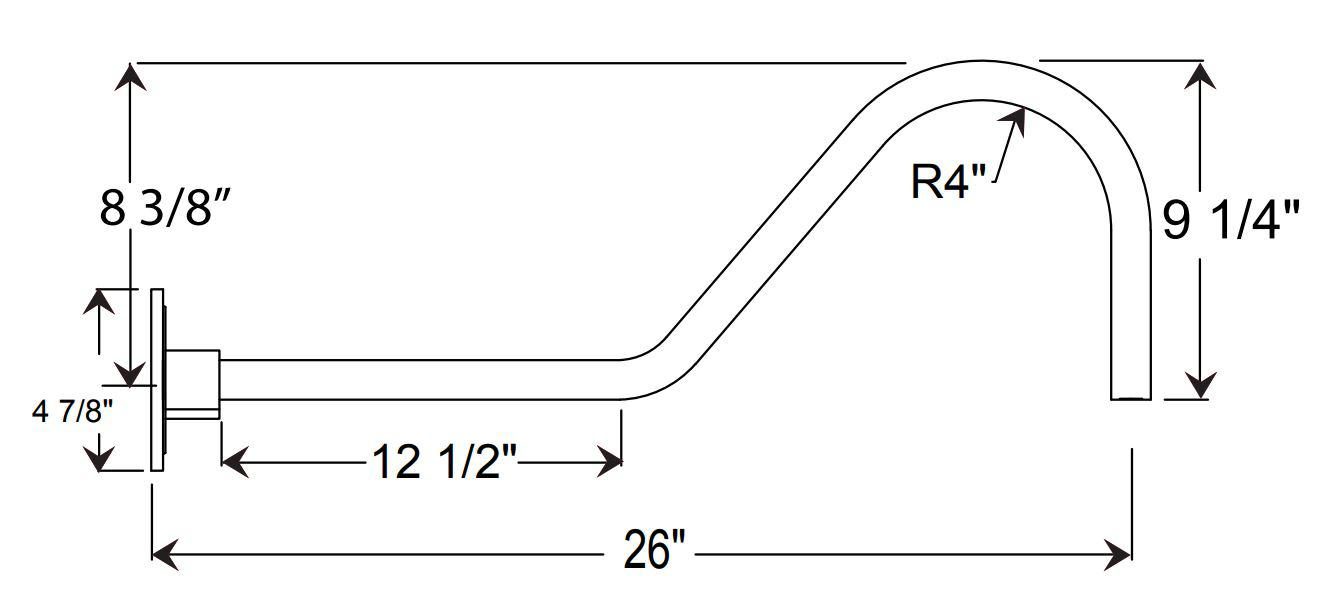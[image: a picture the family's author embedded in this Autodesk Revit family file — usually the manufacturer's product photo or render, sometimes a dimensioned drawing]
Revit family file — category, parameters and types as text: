
# Revit family: SPM- GUP121 MB
name_source: partatom
category: Lighting Fixtures
units: mm (PartAtom-declared; Revit-internal decimal feet)

## family parameters
Always vertical = Yes
Cut with Voids When Loaded = No
Light Source = Yes
OmniClass Number = 23.80.70.00
OmniClass Title = Lighting
Part Type = Normal
Room Calculation Point = No
Round Connector Dimension = Use Diameter
Shared = No
Work Plane-Based = No

## types (1)
- SPM-GUP121
    Apparent Load = 200 VA
    Body Colour = Spun aluminium
    Body Material = body
    Color Filter = 16777215
    Construction Material = Heavy Duty spun aluminum.
    Default Elevation = 0' - 0"
    Description = 120-277 Voltage
    Dimming Lamp Color Temperature Shift = <None>
    Fixture Diameter = 0' - 7"
    Fixture Height = 0' - 9 1/2"
    GLASS = Glass
    Lamp = MED-BASE
    Load Classification = Lighting
    Manufacturer = ANP Lighting
    Model = SPM-GUP121
    Photometric Web File = generic.ies
    Power Factor = 1
    Ring = RING
    SPM-GUP121 = Yes
    Tilt Angle = 90.00°
    URL = https://www.anplighting.com
    Voltage = 277 V
    Warranty = 5 year limited warranty
    Wattage Comments = 200W Max
    Weight = 1.5 lbs

## geometry (parser evidence)
native form markers: Sweep x17
no freeform markers — native parametric forms only
